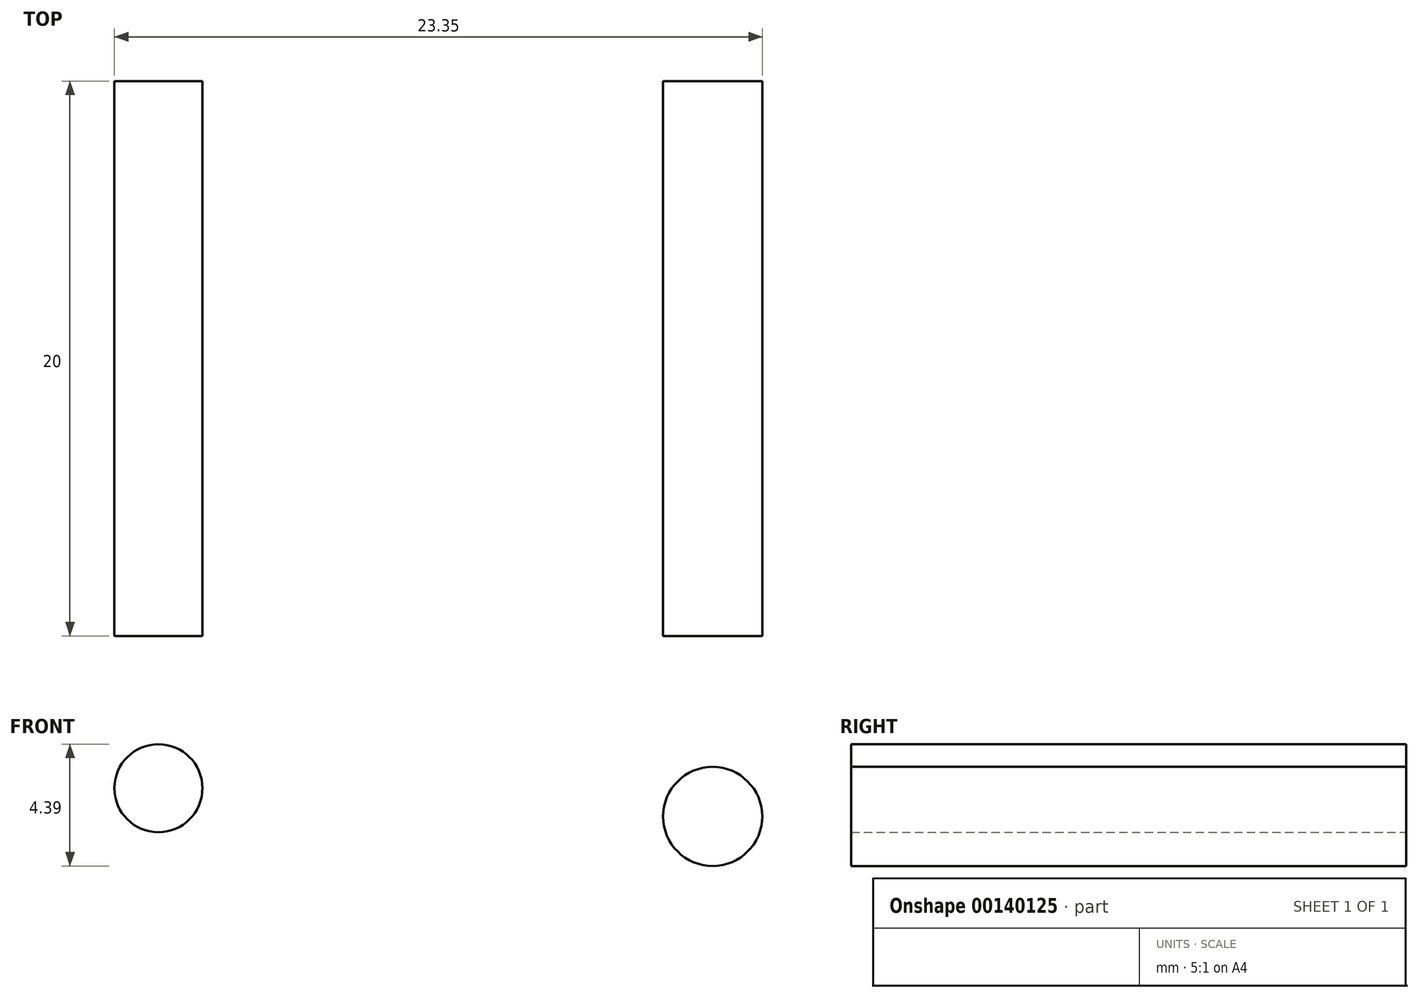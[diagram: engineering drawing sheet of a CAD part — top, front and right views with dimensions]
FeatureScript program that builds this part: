
annotation { "Feature Type Name" : "Feature", "Feature Type Description" : "" }
export const myFeature = defineFeature(function(context is Context, id is Id, definition is map)
    precondition{}
    {
        {
            var Q0;
            Q0=qCreatedBy(makeId("Front.planeOp"),FACE);
            var sketch = newSketch(context, id + "F0", { "sketchPlane" : qUnion([Q0])});
            skCircle(sketch, "E0", {"center": v(-8.47, 47.22) * mm, "radius": 1.59 * mm});
            skCircle(sketch, "E1", {"center": v(11.5, 46.2) * mm, "radius": 1.79 * mm});
            skSolve(sketch);
        }
        {
            var Q0;
            Q0=makeQuery(id+"F0.imprint","IMPRINT",FACE,{"disambiguationData":[TD([[makeQuery(id+"F0.imprint","IMPRINT",EDGE,{"derivedFrom":sQuery(id+"F0.wireOp",EDGE,"E0")}),1.0]])]});
            var Q1;
            Q1=makeQuery(id+"F0.imprint","IMPRINT",FACE,{"disambiguationData":[TD([[makeQuery(id+"F0.imprint","IMPRINT",EDGE,{"derivedFrom":sQuery(id+"F0.wireOp",EDGE,"E1")}),1.0]])]});
            extrude(context, id + "F1", {"entities" : qUnion([Q0, Q1]), "depth" : 20 * mm});
        }
    });
